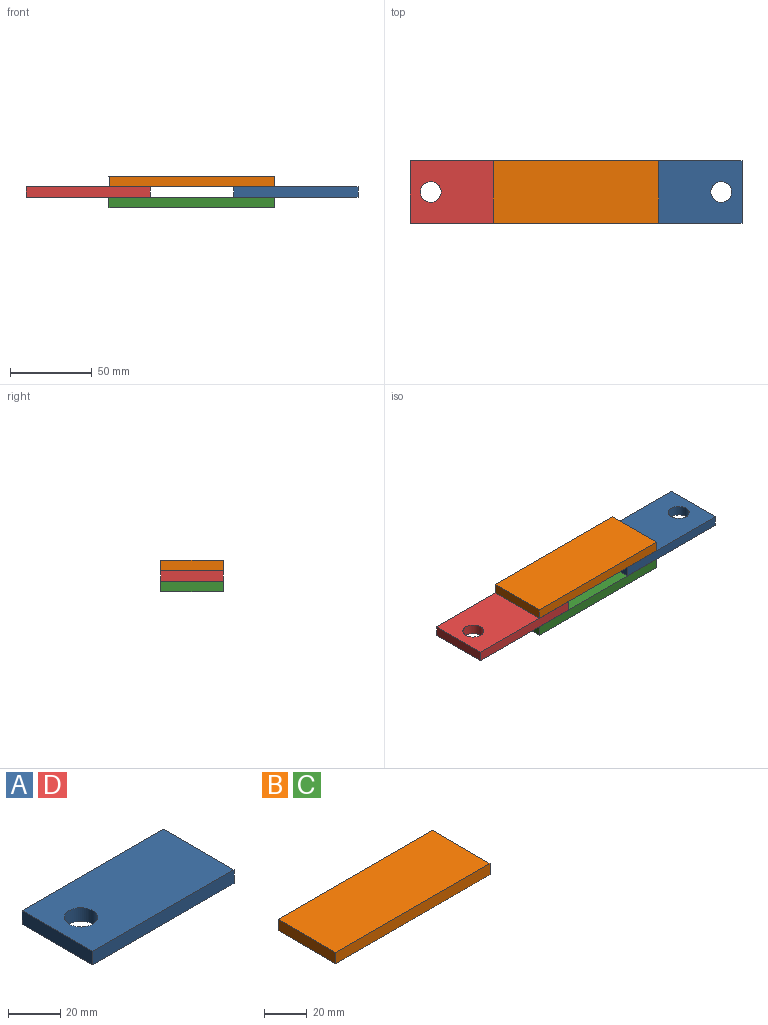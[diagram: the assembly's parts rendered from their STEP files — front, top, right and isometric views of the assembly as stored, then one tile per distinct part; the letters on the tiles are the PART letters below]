
ASSEMBLY  parts=4 mates=5
PART A: 7 faces, bbox 76.2x38.1x6.4 mm
  f0: plane 38.1x6.35mm, normal (1,0,0), area 241.9mm2, adj f1,f3,f4,f5
  f1: plane 76.2x6.35mm, normal (0,1,0), area 483.9mm2, adj f0,f2,f4,f5
  f2: plane 38.1x6.35mm, normal (-1,0,0), area 241.9mm2, adj f1,f3,f4,f5
  f3: plane 76.2x6.35mm, normal (0,-1,0), area 483.9mm2, adj f0,f2,f4,f5
  f4: plane 76.2x38.1mm, normal (0,0,1), area 2776.5mm2, adj f0,f1,f2,f3,f6
  f5: plane 76.2x38.1mm, normal (0,0,-1), area 2776.5mm2, adj f0,f1,f2,f3,f6
  f6: cylinder r=6.35mm len=12.7mm, axis (0,0,1), area 253.4mm2, adj f4,f5
PART B: 6 faces, bbox 101.6x38.1x6.4 mm
  f0: plane 38.1x6.35mm, normal (1,0,0), area 241.9mm2, adj f1,f3,f4,f5
  f1: plane 101.6x6.35mm, normal (0,1,0), area 645.2mm2, adj f0,f2,f4,f5
  f2: plane 38.1x6.35mm, normal (-1,0,0), area 241.9mm2, adj f1,f3,f4,f5
  f3: plane 101.6x6.35mm, normal (0,-1,0), area 645.2mm2, adj f0,f2,f4,f5
  f4: plane 101.6x38.1mm, normal (0,0,1), area 3871mm2, adj f0,f1,f2,f3
  f5: plane 101.6x38.1mm, normal (0,0,-1), area 3871mm2, adj f0,f1,f2,f3
PART C: same geometry as B
PART D: same geometry as A
PLACE A rot(axis=(0,0,-1),180deg) t=(64.88,-2.47,-1.92)mm
PLACE B t=(1.38,-2.47,4.43)mm
PLACE C t=(1.38,-2.47,-8.27)mm fixed
PLACE D t=(-62.12,-2.47,-1.92)mm
MATE fastened D.f1 <-> C.f1  axis (0,1,0) through (-49.42,16.58,-1.92)mm
MATE fastened A.f3 <-> B.f1  axis (0,1,0) through (52.18,16.58,4.43)mm
MATE planar C.f1 <-> D.f1  axis (0,1,0) through (-49.42,16.58,-5.1)mm
MATE planar C.f4 <-> D.f5  axis (0,0,1) through (1.38,-2.47,-1.92)mm
MATE fastened A.f3 <-> C.f1  axis (0,1,0) through (52.18,16.58,-1.92)mm
